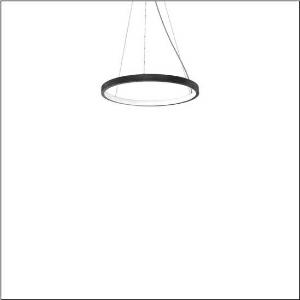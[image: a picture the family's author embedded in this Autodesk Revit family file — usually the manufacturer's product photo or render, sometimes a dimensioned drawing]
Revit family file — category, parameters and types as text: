
# Revit family: silica_r__21_ring-i_5pjbi1d3104a_e1bb
name_source: partatom
category: Lighting Fixtures
units: mm (PartAtom-declared; Revit-internal decimal feet)

## family parameters
Cut with Voids When Loaded = No
Host = Face
Light Source = No
Part Type = Normal
Room Calculation Point = No
Round Connector Dimension = Use Diameter
Shared = No

## types (1)
- Silica® 21 Ring-I (1 x LED, 3510 lm, 60 W, 4000K)
    Apparent Load = 60 VA
    CIE Flux Codes = 22 48 76 50 101
    Color Rendering = 80
    Color Temperature = 4000K
    Default Elevation = 1800 mm
    Description = Silica® 21 Ring-I, suspended luminaire, of PMMA, frosted, light emission: inner ring side luminous distribution, primary light characteristic: symmetric, installation type: suspended mounting, LED, rated luminous flux: 3.510lm, luminous efficacy: 59lm/W, light colour: 840, colour temperature: 4000K, control gear: DALI 2, with terminal, 5-pole, mains connection: 230V, AC/DC, 0/50..60Hz, rated input power: 60W, housing, of extruded aluminium section, jet black (RAL 9005), diameter: 610mm, ceiling canopy, jet black (RAL 9005), protection rating (lamp compartment): IP40, insulation class (complete): insulation class I (protective earthing), certification: CE, impact resistance: IK02, permissible operating ambient temperature: 0..+35°C, packaging unit: 1 piece
    Height = 48 mm  [stored 0.15748 ft]
    Lamp = 1 x LED
    Lamp Light Flux = 3510 lm
    Lamp Power = 60 W
    Lamp count = 1
    Length = 610 mm
    Luminous efficacy = 59 lm/W
    Manufacturer = Siteco
    ModVariant = No
    Model = 5PJBI1D3104A
    Mounting Place = Ceiling
    Mounting Type = Pendant
    Number of Poles = 1
    OnlyDefault = Yes
    Power Factor = 1
    Product Name = Silica® 21 Ring-I
    Product group = suspended luminaire
    ProductGroupID = 905
    Protection Class = Protection class I
    Protection Degree = IP 40
    RLX_Detail_Level = 1
    RLX_Emergency_Light_Flux = 0 lm
    RLX_Emergency_Type = 0
    RLX_Emergency_Type_DB = No
    RlxData = <blob elided: 12373 chars, md5=cec7c4a4>
    Socket = socket
    Standby Power = 0 W
    System Light Flux = 3510 lm
    System Power = 60 W
    Type Comments = Product without accessories
    Type Image = l_1258361.jpg
    URL = http://relux.com
    VarID = ---
    Voltage = 0 V
    Weight = 0.00 kg
    Width = 0 mm  [stored 0 ft]

note: [stored X ft] marks values corroborated as IEEE doubles in the binary element streams (Revit-internal decimal feet)

## geometry (parser evidence)
native form markers: Sweep x12
no freeform markers — native parametric forms only
